# Revit family: Hager-Univers-IP55-D275-H2050-Cl.II-Steel_encl-PL-pl
name_source: partatom
category: Equipement électrique
units: mm (PartAtom-declared; Revit-internal decimal feet)

## family parameters
Configuration du panneau = Deux colonnes, circuits au sein
Cote de connecteur circulaire = Utiliser le diamètre
Couper avec des vides une fois chargée = Non
Hôte = Face
Partagée = Non
Point de calcul de pièce = Non
Type d'élément = Tableau de raccordement

## types (11) — shared parameters
Commentaires du type = Univers
EF000003 - Sposób montażu = EV012274 - Montaż podłogowy
EF000007 - Kolor = EV000270 - Szary
EF000040 - Wysokość = 2050 mm  [stored 6.72572 ft]
EF000049 - Głębokość = 275 mm  [stored 0.902231 ft]
EF000116 - Numer RAL = 7035
EF000118 - Z płytą montażową = Non
EF000266 - Liczba rzędów = 12
EF000339 - Rodzaj pokrywy = EV004216 - Drzwi
EF001088 - Możliwość rozbudowy = Oui
EF001131 - Głębokość wewnętrzna = 275 mm  [stored 0.902231 ft]
EF001596 - Materiał obudowy = EV000179 - Stal
EF001613 - Podtrzymanie funkcji = EV000494 - Brak
EF002950 - Szerokość wyrażona liczbą modułów = 24
EF003532 - Do zastosowań zewnętrznych = Non
EF004293 - Odporność udarowa = EV008784 - IK10
EF005474 - Stopień ochrony (IP) = EV006420 - IP55
EF006306 - Z zamkiem = Non
EF007800 - Do ochrony odgromowej = Non
EF008873 - Prąd znamionowy (In) = 800 A
EF009170 - Obudowa z materiału o wysokiej wytrzymałości mechanicznej = 2 mm  [stored 0.00656168 ft]
EF009171 - Drzwi/pokrywa z materiału o wysokiej wytrzymałości mechanicznej = 2 mm  [stored 0.00656168 ft]
EF009212 - Wykonanie pokrywy = EV000116 - Zamknięty
EF015940 - Pokrywa z wyzwalaczem nadciśnieniowym = Non
Fabricant = Hager
HG000002 - Z drzwiami lub pokrywą = Oui
HG000003 - Zakres = Univers
HG000006 - Montaż podtynkowy = Non
HG000023 - Obudowa dwusekcyjna = Non
HG000024 - Wysokość części dolnej = 800 mm  [stored 2.62467 ft]
HG000026 - Stojąca = Oui
HG000027 - Wysokość cokołu = 200 mm  [stored 0.656168 ft]
zero-valued in all types: EF000218 - Głębokość wbudowania, Elévation par défaut

## per-type parameters (varying)
| type | EF000008 - Szerokość | EF000437 - Liczba wejść kablowych | EF004427 - Liczba modułów | EF004464 - Rodzaj drzwi | EF006244 - Transparentna pokrywa/drzwi | EF009554 - Liczba otworów pod flansze | HG000004 - Referencja producenta | HG000009 - Drzwi dwuskrzydłowe | HG000010 - Drzwi asymetryczne |
| Montaż podłogowy IP55 S1050 W2050 G275  - FR24L2 | 1050 mm | 8 | 576 | EV003602 - Podwójny | Oui | 8 | FR24L2 | Oui | Oui |
| Montaż podłogowy IP55 S1050 W2050 G275  - FR24S2 | 1050 mm | 8 | 576 | EV003602 - Podwójny | Non | 8 | FR24S2 | Oui | Oui |
| Montaż podłogowy IP55 S1300 W2050 G275  - FR25L2 | 1300 mm  [stored 4.26509 ft] | 10 | 720 | EV003602 - Podwójny | Oui | 10 | FR25L2 | Oui | Oui |
| Montaż podłogowy IP55 S1300 W2050 G275  - FR25S2 | 1300 mm  [stored 4.26509 ft] | 10 | 720 | EV003602 - Podwójny | Non | 10 | FR25S2 | Oui | Oui |
| Montaż podłogowy IP55 S1550 W2050 G275  - FR26L2 | 1550 mm  [stored 5.0853 ft] | 12 | 864 | EV003602 - Podwójny | Oui | 12 | FR26L2 | Oui | Oui |
| Montaż podłogowy IP55 S1550 W2050 G275  - FR26S2 | 1550 mm  [stored 5.0853 ft] | 12 | 864 | EV003602 - Podwójny | Non | 12 | FR26S2 | Oui | Oui |
| Montaż podłogowy IP55 S300 W2050 G275  - FR21S2 | 300 mm | 2 | 144 | EV002646 - Pojedynczy | Non | 2 | FR21S2 | Non | Non |
| Montaż podłogowy IP55 S550 W2050 G275  - FR22L2 | 550 mm | 4 | 288 | EV002646 - Pojedynczy | Oui | 4 | FR22L2 | Non | Non |
| Montaż podłogowy IP55 S550 W2050 G275  - FR22S2 | 550 mm | 4 | 288 | EV002646 - Pojedynczy | Non | 4 | FR22S2 | Non | Non |
| Montaż podłogowy IP55 S800 W2050 G275  - FR23L2 | 800 mm  [stored 2.62467 ft] | 6 | 432 | EV002646 - Pojedynczy | Oui | 6 | FR23L2 | Non | Non |
| Montaż podłogowy IP55 S800 W2050 G275  - FR23S2 | 800 mm  [stored 2.62467 ft] | 6 | 432 | EV002646 - Pojedynczy | Non | 6 | FR23S2 | Non | Non |

note: [stored X ft] marks values corroborated as IEEE doubles in the binary element streams (Revit-internal decimal feet)

## geometry (parser evidence)
native form markers: Sweep x10
no freeform markers — native parametric forms only
